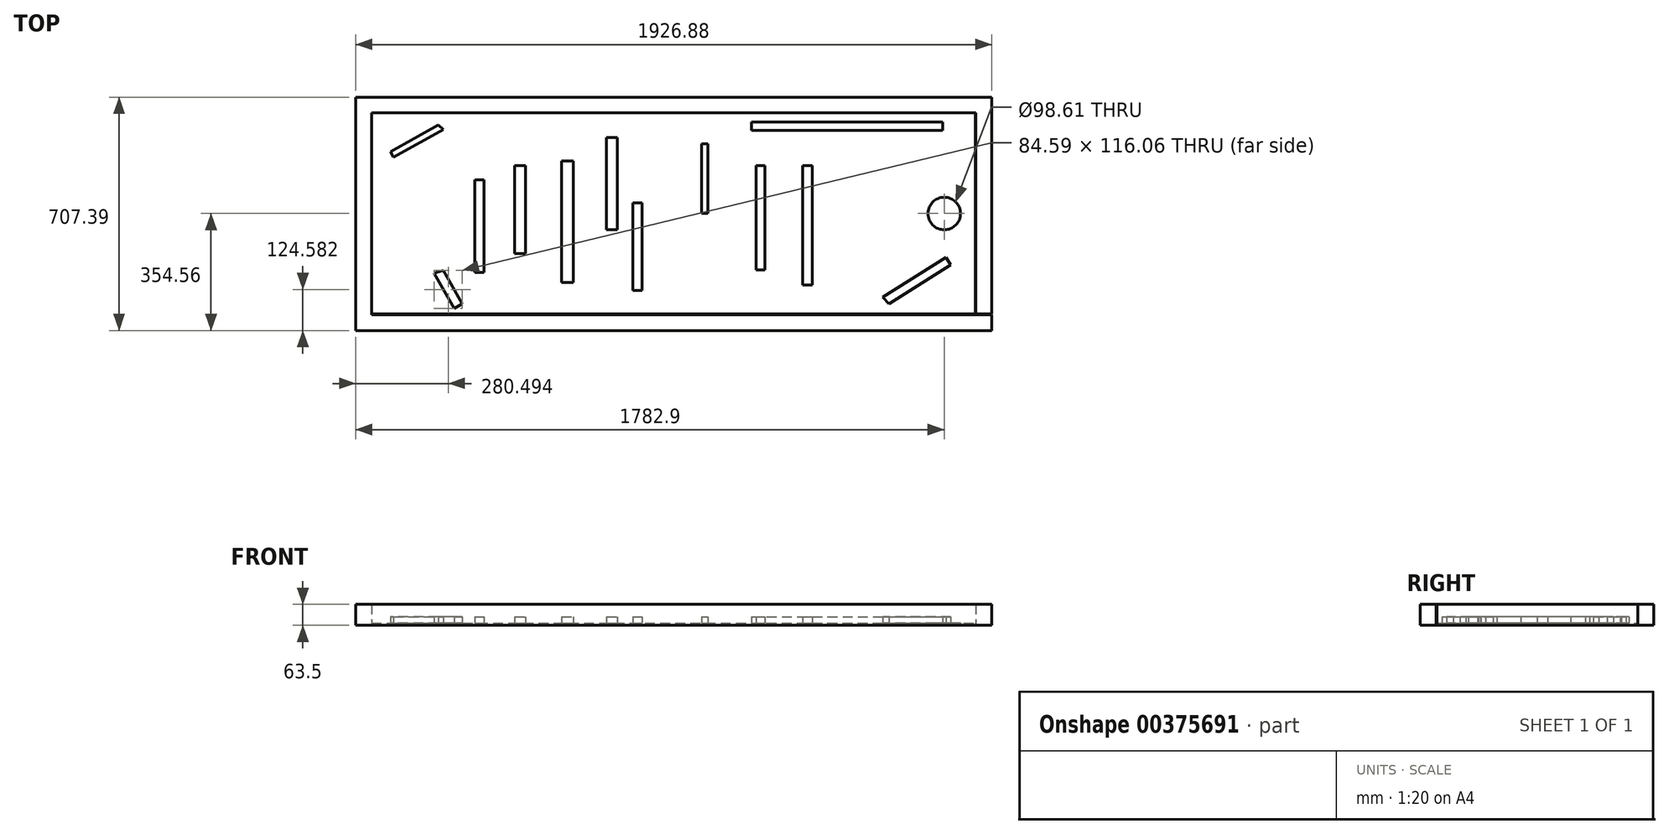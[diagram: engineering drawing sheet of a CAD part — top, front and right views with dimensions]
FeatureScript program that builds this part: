
annotation { "Feature Type Name" : "Feature", "Feature Type Description" : "" }
export const myFeature = defineFeature(function(context is Context, id is Id, definition is map)
    precondition{}
    {
        {
            var Q0;
            Q0=qCreatedBy(makeId("Top.planeOp"),FACE);
            var sketch = newSketch(context, id + "F0", { "sketchPlane" : qUnion([Q0])});
            skLineSegment(sketch, "E0.bottom", {"start": v(-914.4, -304.8) * mm, "end": v(914.4, -304.8) * mm});
            skLineSegment(sketch, "E0.left", {"start": v(-914.4, -304.8) * mm, "end": v(-914.4, 304.8) * mm});
            skLineSegment(sketch, "E0.right", {"start": v(914.4, -304.8) * mm, "end": v(914.4, 304.8) * mm});
            skCircle(sketch, "E1", {"center": v(820.46, 0) * mm, "radius": 49.3 * mm});
            skPoint(sketch, "E1.centerSnap0", {"position": v(-914.4, 0) * mm});
            skLineSegment(sketch, "E2.bottom", {"start": v(-914.4, 304.8) * mm, "end": v(-962.44, 304.8) * mm});
            skLineSegment(sketch, "E2.top", {"start": v(-914.4, -306.53) * mm, "end": v(-962.44, -306.53) * mm});
            skLineSegment(sketch, "E2.left", {"start": v(-914.4, 304.8) * mm, "end": v(-914.4, -306.53) * mm});
            skLineSegment(sketch, "E2.right", {"start": v(-962.44, 304.8) * mm, "end": v(-962.44, -306.53) * mm});
            skLineSegment(sketch, "E3.bottom", {"start": v(-962.44, 304.8) * mm, "end": v(-914.4, 304.8) * mm});
            skLineSegment(sketch, "E4.trimOffspring", {"start": v(914.4, 304.8) * mm, "end": v(916.33, 304.8) * mm});
            skLineSegment(sketch, "E5.bottom", {"start": v(916.33, 304.8) * mm, "end": v(964.36, 304.8) * mm});
            skLineSegment(sketch, "E5.top", {"start": v(916.33, -303.83) * mm, "end": v(964.36, -303.83) * mm});
            skLineSegment(sketch, "E5.left", {"start": v(916.33, 304.8) * mm, "end": v(916.33, -303.83) * mm});
            skLineSegment(sketch, "E5.right", {"start": v(964.36, 304.8) * mm, "end": v(964.36, -303.83) * mm});
            skLineSegment(sketch, "E6.bottom", {"start": v(-962.44, 304.8) * mm, "end": v(964.44, 304.8) * mm});
            skLineSegment(sketch, "E6.top", {"start": v(-962.44, 352.83) * mm, "end": v(964.44, 352.83) * mm});
            skLineSegment(sketch, "E6.left", {"start": v(-962.44, 304.8) * mm, "end": v(-962.44, 352.83) * mm});
            skLineSegment(sketch, "E6.right", {"start": v(964.44, 304.8) * mm, "end": v(964.44, 352.83) * mm});
            skLineSegment(sketch, "E7.bottom", {"start": v(-962.44, -306.53) * mm, "end": v(964.44, -306.53) * mm});
            skLineSegment(sketch, "E7.top", {"start": v(-962.44, -354.56) * mm, "end": v(964.44, -354.56) * mm});
            skLineSegment(sketch, "E7.left", {"start": v(-962.44, -306.53) * mm, "end": v(-962.44, -354.56) * mm});
            skLineSegment(sketch, "E7.right", {"start": v(964.44, -306.53) * mm, "end": v(964.44, -354.56) * mm});
            skLineSegment(sketch, "E8.bottom", {"start": v(-601.8, 101.96) * mm, "end": v(-573.4, 101.96) * mm});
            skLineSegment(sketch, "E8.top", {"start": v(-601.8, -178.2) * mm, "end": v(-573.4, -178.2) * mm});
            skLineSegment(sketch, "E8.left", {"start": v(-601.8, 101.96) * mm, "end": v(-601.8, -178.2) * mm});
            skLineSegment(sketch, "E8.right", {"start": v(-573.4, 101.96) * mm, "end": v(-573.4, -178.2) * mm});
            skLineSegment(sketch, "E9.bottom", {"start": v(-480.64, 145.5) * mm, "end": v(-448.46, 145.5) * mm});
            skLineSegment(sketch, "E9.top", {"start": v(-480.64, -121.42) * mm, "end": v(-448.46, -121.42) * mm});
            skLineSegment(sketch, "E9.left", {"start": v(-480.64, 145.5) * mm, "end": v(-480.64, -121.42) * mm});
            skLineSegment(sketch, "E9.right", {"start": v(-448.46, 145.5) * mm, "end": v(-448.46, -121.42) * mm});
            skLineSegment(sketch, "E10.bottom", {"start": v(-338.66, 158.75) * mm, "end": v(-302.7, 158.75) * mm});
            skLineSegment(sketch, "E10.top", {"start": v(-338.66, -208.5) * mm, "end": v(-302.7, -208.5) * mm});
            skLineSegment(sketch, "E10.left", {"start": v(-338.66, 158.75) * mm, "end": v(-338.66, -208.5) * mm});
            skLineSegment(sketch, "E10.right", {"start": v(-302.7, 158.75) * mm, "end": v(-302.7, -208.5) * mm});
            skLineSegment(sketch, "E11.bottom", {"start": v(-202.36, 230.7) * mm, "end": v(-170.18, 230.7) * mm});
            skLineSegment(sketch, "E11.top", {"start": v(-202.36, -49.48) * mm, "end": v(-170.18, -49.48) * mm});
            skLineSegment(sketch, "E11.left", {"start": v(-202.36, 230.7) * mm, "end": v(-202.36, -49.48) * mm});
            skLineSegment(sketch, "E11.right", {"start": v(-170.18, 230.7) * mm, "end": v(-170.18, -49.48) * mm});
            skLineSegment(sketch, "E12.bottom", {"start": v(-122.85, 31.92) * mm, "end": v(-94.45, 31.92) * mm});
            skLineSegment(sketch, "E12.top", {"start": v(-122.85, -233.1) * mm, "end": v(-94.45, -233.1) * mm});
            skLineSegment(sketch, "E12.left", {"start": v(-122.85, 31.92) * mm, "end": v(-122.85, -233.1) * mm});
            skLineSegment(sketch, "E12.right", {"start": v(-94.45, 31.92) * mm, "end": v(-94.45, -233.1) * mm});
            skLineSegment(sketch, "E13.bottom", {"start": v(85.39, 211.76) * mm, "end": v(104.32, 211.76) * mm});
            skLineSegment(sketch, "E13.top", {"start": v(85.39, 0) * mm, "end": v(104.32, 0) * mm});
            skLineSegment(sketch, "E13.left", {"start": v(85.39, 211.76) * mm, "end": v(85.39, 0) * mm});
            skLineSegment(sketch, "E13.right", {"start": v(104.32, 211.76) * mm, "end": v(104.32, 0) * mm});
            skLineSegment(sketch, "E14.bottom", {"start": v(250.08, 145.5) * mm, "end": v(276.58, 145.5) * mm});
            skLineSegment(sketch, "E14.top", {"start": v(250.08, -170.64) * mm, "end": v(276.58, -170.64) * mm});
            skLineSegment(sketch, "E14.left", {"start": v(250.08, 145.5) * mm, "end": v(250.08, -170.64) * mm});
            skLineSegment(sketch, "E14.right", {"start": v(276.58, 145.5) * mm, "end": v(276.58, -170.64) * mm});
            skLineSegment(sketch, "E15.bottom", {"start": v(236.83, 278.02) * mm, "end": v(816.1, 278.02) * mm});
            skLineSegment(sketch, "E15.top", {"start": v(236.83, 251.51) * mm, "end": v(816.1, 251.51) * mm});
            skLineSegment(sketch, "E15.left", {"start": v(236.83, 278.02) * mm, "end": v(236.83, 251.51) * mm});
            skLineSegment(sketch, "E15.right", {"start": v(816.1, 278.02) * mm, "end": v(816.1, 251.51) * mm});
            skLineSegment(sketch, "E16", {"start": v(634.37, -253.93) * mm, "end": v(825.57, -132.78) * mm});
            skLineSegment(sketch, "E17", {"start": v(825.57, -132.78) * mm, "end": v(840.1, -155.7) * mm});
            skLineSegment(sketch, "E18", {"start": v(840.1, -155.7) * mm, "end": v(652.99, -274.26) * mm});
            skLineSegment(sketch, "E19", {"start": v(652.99, -274.26) * mm, "end": v(634.37, -253.93) * mm});
            skLineSegment(sketch, "E20", {"start": v(-711.6, 268.55) * mm, "end": v(-857.36, 187.15) * mm});
            skLineSegment(sketch, "E21", {"start": v(-857.36, 187.15) * mm, "end": v(-848.11, 170.6) * mm});
            skLineSegment(sketch, "E22", {"start": v(-848.11, 170.6) * mm, "end": v(-696.78, 255.11) * mm});
            skLineSegment(sketch, "E23", {"start": v(-696.78, 255.11) * mm, "end": v(-711.6, 268.55) * mm});
            skLineSegment(sketch, "E24", {"start": v(-664.26, -288) * mm, "end": v(-724.24, -180.6) * mm});
            skLineSegment(sketch, "E25", {"start": v(-664.26, -288) * mm, "end": v(-639.65, -274.26) * mm});
            skLineSegment(sketch, "E26", {"start": v(-639.65, -274.26) * mm, "end": v(-696.78, -171.95) * mm});
            skLineSegment(sketch, "E27", {"start": v(-696.78, -171.95) * mm, "end": v(-724.24, -180.6) * mm});
            skLineSegment(sketch, "E28.bottom", {"start": v(392.06, 145.5) * mm, "end": v(420.46, 145.5) * mm});
            skLineSegment(sketch, "E28.top", {"start": v(392.06, -216.07) * mm, "end": v(420.46, -216.07) * mm});
            skLineSegment(sketch, "E28.left", {"start": v(392.06, 145.5) * mm, "end": v(392.06, -216.07) * mm});
            skLineSegment(sketch, "E28.right", {"start": v(420.46, 145.5) * mm, "end": v(420.46, -216.07) * mm});
            skSolve(sketch);
        }
        {
            var Q0;
            Q0=qCreatedBy(makeId("Front.planeOp"),FACE);
            var sketch = newSketch(context, id + "F1", { "sketchPlane" : qUnion([Q0])});
            skArc(sketch, "E29", {"start": v(543.46, 0) * mm, "mid": v(522.93, 22.44) * mm, "end": v(502.4, 0) * mm});
            skSolve(sketch);
        }
        {
            var Q0;
            Q0=makeQuery(id+"F0.imprint","IMPRINT",FACE,{"disambiguationData":[TD([[makeQuery(id+"F0.imprint","IMPRINT",EDGE,{"derivedFrom":sQuery(id+"F0.wireOp",EDGE,"E24")}),-1.0]])]});
            extrude(context, id + "F2", {"entities" : qUnion([Q0]), "depth" : 25.4 * mm});
        }
        {
            var Q0;
            {var subQ0=sQuery(id+"F0.wireOp",EDGE,"E2.right");Q0=makeQuery(id+"F0.imprint","IMPRINT",FACE,{"disambiguationData":[TD([[makeQuery(id+"F0.imprint","IMPRINT",EDGE,{"derivedFrom":subQ0}),1.0]])]});}
            var Q1;
            Q1=makeQuery(id+"F0.imprint","IMPRINT",FACE,{"disambiguationData":[TD([[makeQuery(id+"F0.imprint","IMPRINT",EDGE,{"derivedFrom":sQuery(id+"F0.wireOp",EDGE,"E7.top")}),1.0]])]});
            var Q2;
            Q2=makeQuery(id+"F0.imprint","IMPRINT",FACE,{"disambiguationData":[TD([[makeQuery(id+"F0.imprint","IMPRINT",EDGE,{"derivedFrom":sQuery(id+"F0.wireOp",EDGE,"E6.top")}),-1.0]])]});
            var Q3;
            Q3=makeQuery(id+"F0.imprint","IMPRINT",FACE,{"disambiguationData":[TD([[makeQuery(id+"F0.imprint","IMPRINT",EDGE,{"derivedFrom":sQuery(id+"F0.wireOp",EDGE,"E5.top")}),1.0]])]});
            extrude(context, id + "F3", {"entities" : qUnion([Q0, Q1, Q2, Q3]), "depth" : 63.5 * mm});
        }
        {
            var Q0;
            {var subQ1=sQuery(id+"F0.wireOp",EDGE,"E0.bottom");Q0=makeQuery(id+"F0.imprint","IMPRINT",FACE,{"disambiguationData":[TD([[makeQuery(id+"F0.imprint","IMPRINT",EDGE,{"derivedFrom":subQ1}),1.0]])]});}
            extrude(context, id + "F4", {"entities" : qUnion([Q0]), "depth" : 6.35 * mm});
        }
        {
            var Q0;
            Q0=makeQuery(id+"F0.imprint","IMPRINT",FACE,{"disambiguationData":[TD([[makeQuery(id+"F0.imprint","IMPRINT",EDGE,{"derivedFrom":sQuery(id+"F0.wireOp",EDGE,"E8.bottom")}),-1.0]])]});
            var Q1;
            Q1=makeQuery(id+"F0.imprint","IMPRINT",FACE,{"disambiguationData":[TD([[makeQuery(id+"F0.imprint","IMPRINT",EDGE,{"derivedFrom":sQuery(id+"F0.wireOp",EDGE,"E20")}),1.0]])]});
            var Q2;
            Q2=makeQuery(id+"F0.imprint","IMPRINT",FACE,{"disambiguationData":[TD([[makeQuery(id+"F0.imprint","IMPRINT",EDGE,{"derivedFrom":sQuery(id+"F0.wireOp",EDGE,"E9.bottom")}),-1.0]])]});
            var Q3;
            Q3=makeQuery(id+"F0.imprint","IMPRINT",FACE,{"disambiguationData":[TD([[makeQuery(id+"F0.imprint","IMPRINT",EDGE,{"derivedFrom":sQuery(id+"F0.wireOp",EDGE,"E10.bottom")}),-1.0]])]});
            var Q4;
            Q4=makeQuery(id+"F0.imprint","IMPRINT",FACE,{"disambiguationData":[TD([[makeQuery(id+"F0.imprint","IMPRINT",EDGE,{"derivedFrom":sQuery(id+"F0.wireOp",EDGE,"E11.bottom")}),-1.0]])]});
            var Q5;
            Q5=makeQuery(id+"F0.imprint","IMPRINT",FACE,{"disambiguationData":[TD([[makeQuery(id+"F0.imprint","IMPRINT",EDGE,{"derivedFrom":sQuery(id+"F0.wireOp",EDGE,"E12.bottom")}),-1.0]])]});
            var Q6;
            Q6=makeQuery(id+"F0.imprint","IMPRINT",FACE,{"disambiguationData":[TD([[makeQuery(id+"F0.imprint","IMPRINT",EDGE,{"derivedFrom":sQuery(id+"F0.wireOp",EDGE,"E13.bottom")}),-1.0]])]});
            var Q7;
            Q7=makeQuery(id+"F0.imprint","IMPRINT",FACE,{"disambiguationData":[TD([[makeQuery(id+"F0.imprint","IMPRINT",EDGE,{"derivedFrom":sQuery(id+"F0.wireOp",EDGE,"E14.bottom")}),-1.0]])]});
            var Q8;
            Q8=makeQuery(id+"F0.imprint","IMPRINT",FACE,{"disambiguationData":[TD([[makeQuery(id+"F0.imprint","IMPRINT",EDGE,{"derivedFrom":sQuery(id+"F0.wireOp",EDGE,"E28.bottom")}),-1.0]])]});
            extrude(context, id + "F5", {"entities" : qUnion([Q0, Q1, Q2, Q3, Q4, Q5, Q6, Q7, Q8]), "operationType" : NewBodyOperationType.ADD, "depth" : 25.4 * mm});
        }
        {
            var Q0;
            Q0=sQuery(id+"F1.wireOp",EDGE,"E29");
            extrude(context, id + "F6", {"bodyType" : ToolBodyType.SURFACE, "surfaceEntities" : qUnion([Q0]), "depth" : 127 * mm, "hasSecondDirection" : true, "secondDirectionOppositeDirection" : true, "secondDirectionDepth" : 127 * mm});
        }
        {
            var Q0;
            Q0=makeQuery(id+"F0.imprint","IMPRINT",FACE,{"disambiguationData":[TD([[makeQuery(id+"F0.imprint","IMPRINT",EDGE,{"derivedFrom":sQuery(id+"F0.wireOp",EDGE,"E15.bottom")}),-1.0]])]});
            extrude(context, id + "F7", {"entities" : qUnion([Q0]), "operationType" : NewBodyOperationType.ADD, "depth" : 25.4 * mm});
        }
        {
            var Q0;
            Q0=makeQuery(id+"F0.imprint","IMPRINT",FACE,{"disambiguationData":[TD([[makeQuery(id+"F0.imprint","IMPRINT",EDGE,{"derivedFrom":sQuery(id+"F0.wireOp",EDGE,"E16")}),-1.0]])]});
            extrude(context, id + "F8", {"entities" : qUnion([Q0]), "operationType" : NewBodyOperationType.ADD, "depth" : 25.4 * mm});
        }
        {
            var Q0;
            Q0=sQuery(id+"F0.wireOp",EDGE,"E1");
            extrude(context, id + "F9", {"bodyType" : ToolBodyType.SURFACE, "surfaceEntities" : qUnion([Q0]), "depth" : 2.54 * mm});
        }
    });
